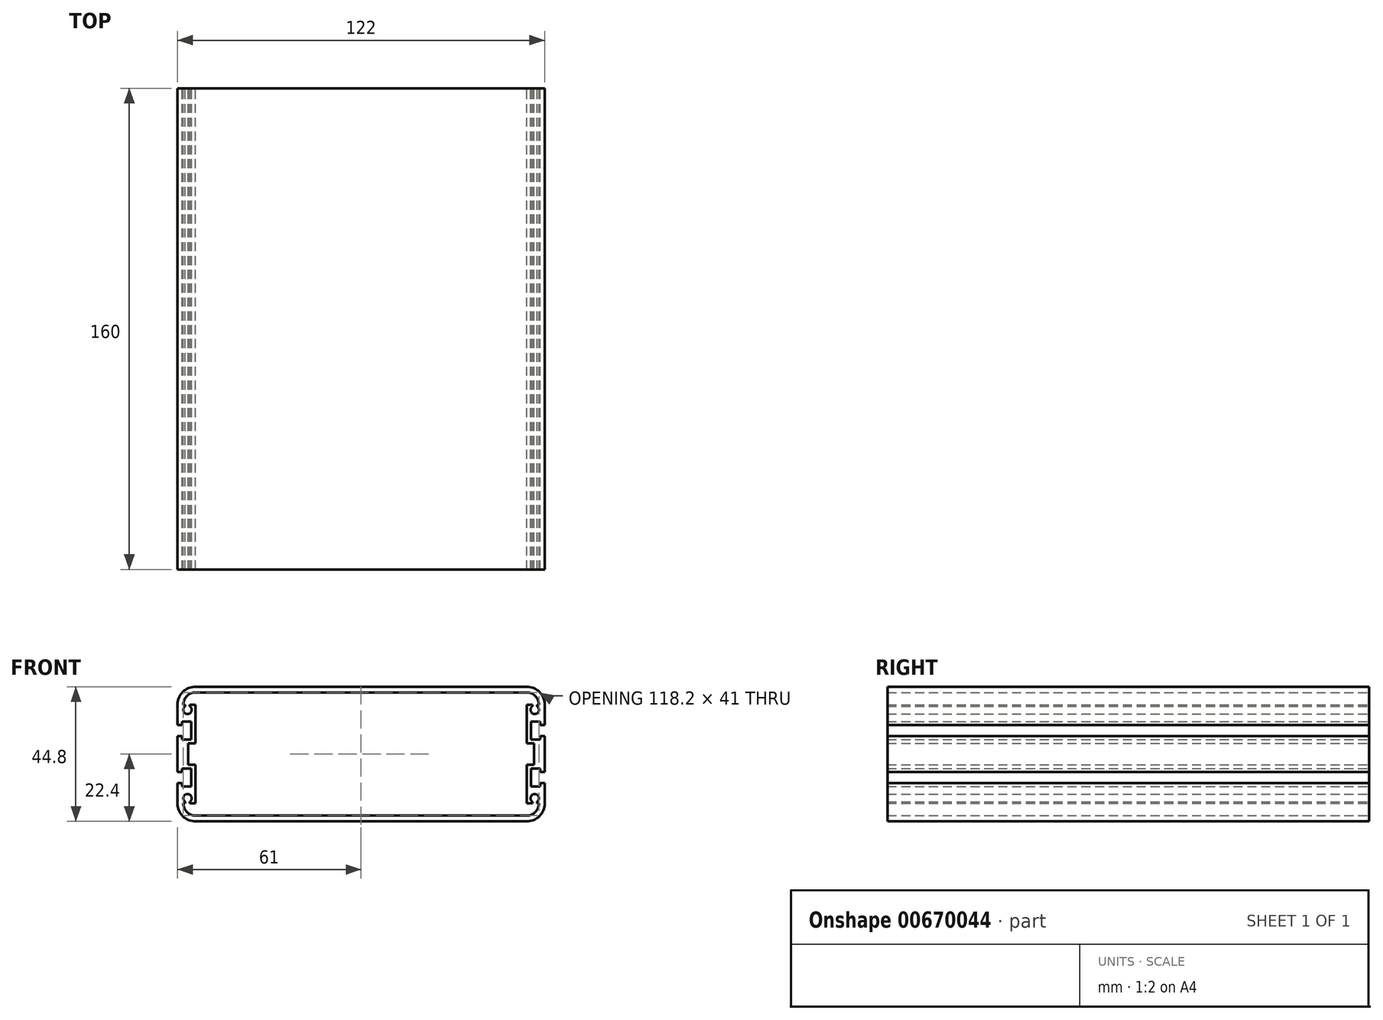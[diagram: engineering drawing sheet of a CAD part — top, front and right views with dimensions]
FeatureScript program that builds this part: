
annotation { "Feature Type Name" : "Feature", "Feature Type Description" : "" }
export const myFeature = defineFeature(function(context is Context, id is Id, definition is map)
    precondition{}
    {
        {
            var Q0;
            Q0=qCreatedBy(makeId("Front.planeOp"),FACE);
            var sketch = newSketch(context, id + "F0", { "sketchPlane" : qUnion([Q0])});
            skLineSegment(sketch, "E0.bottom", {"start": v(0, 0) * mm, "end": v(122, 0) * mm});
            skLineSegment(sketch, "E0.top", {"start": v(6, 44.8) * mm, "end": v(61, 44.8) * mm});
            skLineSegment(sketch, "E0.left", {"start": v(0, 22.4) * mm, "end": v(0, 28.4) * mm});
            skLineSegment(sketch, "E1", {"start": v(61, 44.8) * mm, "end": v(61, 0) * mm, "construction": true});
            skLineSegment(sketch, "E2", {"start": v(0, 22.4) * mm, "end": v(122, 22.4) * mm, "construction": true});
            skLineSegment(sketch, "E3.bottom", {"start": v(6, 42.9) * mm, "end": v(61, 42.9) * mm});
            skLineSegment(sketch, "E3.left", {"start": v(6, 38.8) * mm, "end": v(6, 25.9) * mm});
            skPoint(sketch, "E3.middle", {"position": v(61, 22.4) * mm});
            skPoint(sketch, "E4.visualSharp", {"position": v(0, 44.8) * mm});
            skArc(sketch, "E4.filletArc", {"start": v(6, 44.8) * mm, "mid": v(1.76, 43.04) * mm, "end": v(0, 38.8) * mm});
            skLineSegment(sketch, "E5", {"start": v(0, 32) * mm, "end": v(1.5, 32) * mm});
            skLineSegment(sketch, "E6", {"start": v(1.5, 32) * mm, "end": v(1.5, 33.2) * mm});
            skLineSegment(sketch, "E7", {"start": v(1.5, 33.2) * mm, "end": v(4.5, 33.2) * mm});
            skLineSegment(sketch, "E8", {"start": v(4.5, 33.2) * mm, "end": v(4.5, 27.2) * mm});
            skLineSegment(sketch, "E9", {"start": v(4.5, 27.2) * mm, "end": v(1.5, 27.2) * mm});
            skLineSegment(sketch, "E10", {"start": v(1.5, 27.2) * mm, "end": v(1.5, 28.4) * mm});
            skLineSegment(sketch, "E11", {"start": v(1.5, 28.4) * mm, "end": v(0, 28.4) * mm});
            skLineSegment(sketch, "E12.trimOffspring", {"start": v(0, 32) * mm, "end": v(0, 38.8) * mm});
            skArc(sketch, "E13", {"start": v(2.55, 38.28) * mm, "mid": v(3.3, 35.7) * mm, "end": v(4.05, 38.28) * mm});
            skArc(sketch, "E14", {"start": v(6, 42.9) * mm, "mid": v(3.1, 41.7) * mm, "end": v(1.9, 38.8) * mm});
            skLineSegment(sketch, "E15", {"start": v(1.9, 38.8) * mm, "end": v(2.55, 38.8) * mm});
            skLineSegment(sketch, "E16", {"start": v(2.55, 38.8) * mm, "end": v(2.55, 38.28) * mm});
            skLineSegment(sketch, "E17", {"start": v(4.05, 38.28) * mm, "end": v(4.05, 38.8) * mm});
            skLineSegment(sketch, "E18", {"start": v(4.05, 38.8) * mm, "end": v(6, 38.8) * mm});
            skLineSegment(sketch, "E19", {"start": v(3.3, 37.1) * mm, "end": v(3.3, 38.82) * mm, "construction": true});
            skLineSegment(sketch, "E20", {"start": v(3.5, 22.4) * mm, "end": v(3.5, 25.9) * mm});
            skLineSegment(sketch, "E21", {"start": v(3.5, 25.9) * mm, "end": v(6, 25.9) * mm});
            skLineSegment(sketch, "E22.MirrorCS", {"start": v(117.95, 38.28) * mm, "end": v(117.95, 38.8) * mm});
            skLineSegment(sketch, "E23.MirrorCS", {"start": v(119.45, 38.8) * mm, "end": v(119.45, 38.28) * mm});
            skLineSegment(sketch, "E24.MirrorCS", {"start": v(118.7, 37.1) * mm, "end": v(118.7, 38.82) * mm, "construction": true});
            skLineSegment(sketch, "E25.MirrorCS", {"start": v(120.1, 38.8) * mm, "end": v(119.45, 38.8) * mm});
            skLineSegment(sketch, "E26.MirrorCS", {"start": v(117.95, 38.8) * mm, "end": v(116, 38.8) * mm});
            skLineSegment(sketch, "E27.MirrorCS", {"start": v(122, 32) * mm, "end": v(120.5, 32) * mm});
            skArc(sketch, "E28.MirrorCS", {"start": v(119.45, 38.28) * mm, "mid": v(118.7, 35.7) * mm, "end": v(117.95, 38.28) * mm});
            skLineSegment(sketch, "E29.MirrorCS", {"start": v(120.5, 27.2) * mm, "end": v(120.5, 28.4) * mm});
            skLineSegment(sketch, "E30.MirrorCS", {"start": v(120.5, 32) * mm, "end": v(120.5, 33.2) * mm});
            skLineSegment(sketch, "E31.MirrorCS", {"start": v(120.5, 28.4) * mm, "end": v(122, 28.4) * mm});
            skLineSegment(sketch, "E32.MirrorCS", {"start": v(117.5, 27.2) * mm, "end": v(120.5, 27.2) * mm});
            skLineSegment(sketch, "E33.MirrorCS", {"start": v(120.5, 33.2) * mm, "end": v(117.5, 33.2) * mm});
            skLineSegment(sketch, "E34.MirrorCS", {"start": v(122, 32) * mm, "end": v(122, 38.8) * mm});
            skLineSegment(sketch, "E35.MirrorCS", {"start": v(118.5, 25.9) * mm, "end": v(116, 25.9) * mm});
            skLineSegment(sketch, "E36.MirrorCS", {"start": v(122, 22.4) * mm, "end": v(122, 28.4) * mm});
            skLineSegment(sketch, "E37.MirrorCS", {"start": v(117.5, 33.2) * mm, "end": v(117.5, 27.2) * mm});
            skArc(sketch, "E38.MirrorCS", {"start": v(116, 42.9) * mm, "mid": v(118.9, 41.7) * mm, "end": v(120.1, 38.8) * mm});
            skArc(sketch, "E39.MirrorCS", {"start": v(116, 44.8) * mm, "mid": v(120.24, 43.04) * mm, "end": v(122, 38.8) * mm});
            skLineSegment(sketch, "E40.MirrorCS", {"start": v(118.5, 22.4) * mm, "end": v(118.5, 25.9) * mm});
            skLineSegment(sketch, "E41.MirrorCS", {"start": v(116, 42.9) * mm, "end": v(61, 42.9) * mm});
            skLineSegment(sketch, "E42.MirrorCS", {"start": v(116, 38.8) * mm, "end": v(116, 25.9) * mm});
            skPoint(sketch, "E43.MirrorP", {"position": v(122, 44.8) * mm});
            skLineSegment(sketch, "E44.MirrorCS", {"start": v(116, 44.8) * mm, "end": v(61, 44.8) * mm});
            skLineSegment(sketch, "E45.MirrorCS", {"start": v(122, 22.4) * mm, "end": v(0, 22.4) * mm, "construction": true});
            skLineSegment(sketch, "E46.MirrorCS", {"start": v(2.55, 6) * mm, "end": v(2.55, 6.52) * mm});
            skLineSegment(sketch, "E47.MirrorCS", {"start": v(4.05, 6.52) * mm, "end": v(4.05, 6) * mm});
            skLineSegment(sketch, "E48.MirrorCS", {"start": v(3.3, 7.7) * mm, "end": v(3.3, 5.98) * mm, "construction": true});
            skLineSegment(sketch, "E49.MirrorCS", {"start": v(117.95, 6.52) * mm, "end": v(117.95, 6) * mm});
            skLineSegment(sketch, "E50.MirrorCS", {"start": v(1.9, 6) * mm, "end": v(2.55, 6) * mm});
            skLineSegment(sketch, "E51.MirrorCS", {"start": v(119.45, 6) * mm, "end": v(119.45, 6.52) * mm});
            skLineSegment(sketch, "E52.MirrorCS", {"start": v(117.95, 6) * mm, "end": v(116, 6) * mm});
            skLineSegment(sketch, "E53.MirrorCS", {"start": v(120.1, 6) * mm, "end": v(119.45, 6) * mm});
            skLineSegment(sketch, "E54.MirrorCS", {"start": v(0, 12.8) * mm, "end": v(1.5, 12.8) * mm});
            skLineSegment(sketch, "E55.MirrorCS", {"start": v(1.5, 17.6) * mm, "end": v(1.5, 16.4) * mm});
            skLineSegment(sketch, "E56.MirrorCS", {"start": v(1.5, 16.4) * mm, "end": v(0, 16.4) * mm});
            skLineSegment(sketch, "E57.MirrorCS", {"start": v(1.5, 12.8) * mm, "end": v(1.5, 11.6) * mm});
            skLineSegment(sketch, "E58.MirrorCS", {"start": v(4.05, 6) * mm, "end": v(6, 6) * mm});
            skLineSegment(sketch, "E59.MirrorCS", {"start": v(118.7, 7.7) * mm, "end": v(118.7, 5.98) * mm, "construction": true});
            skLineSegment(sketch, "E60.MirrorCS", {"start": v(122, 12.8) * mm, "end": v(120.5, 12.8) * mm});
            skArc(sketch, "E61.MirrorCS", {"start": v(2.55, 6.52) * mm, "mid": v(3.3, 9.1) * mm, "end": v(4.05, 6.52) * mm});
            skLineSegment(sketch, "E62.MirrorCS", {"start": v(120.5, 17.6) * mm, "end": v(120.5, 16.4) * mm});
            skLineSegment(sketch, "E63.MirrorCS", {"start": v(120.5, 12.8) * mm, "end": v(120.5, 11.6) * mm});
            skLineSegment(sketch, "E64.MirrorCS", {"start": v(4.5, 17.6) * mm, "end": v(1.5, 17.6) * mm});
            skLineSegment(sketch, "E65.MirrorCS", {"start": v(120.5, 16.4) * mm, "end": v(122, 16.4) * mm});
            skLineSegment(sketch, "E66.MirrorCS", {"start": v(1.5, 11.6) * mm, "end": v(4.5, 11.6) * mm});
            skLineSegment(sketch, "E67.MirrorCS", {"start": v(3.5, 18.9) * mm, "end": v(6, 18.9) * mm});
            skLineSegment(sketch, "E68.MirrorCS", {"start": v(120.5, 11.6) * mm, "end": v(117.5, 11.6) * mm});
            skLineSegment(sketch, "E69.MirrorCS", {"start": v(117.5, 17.6) * mm, "end": v(120.5, 17.6) * mm});
            skLineSegment(sketch, "E70.MirrorCS", {"start": v(122, 22.4) * mm, "end": v(122, 16.4) * mm});
            skLineSegment(sketch, "E71.MirrorCS", {"start": v(6, 6) * mm, "end": v(6, 18.9) * mm});
            skArc(sketch, "E72.MirrorCS", {"start": v(119.45, 6.52) * mm, "mid": v(118.7, 9.1) * mm, "end": v(117.95, 6.52) * mm});
            skLineSegment(sketch, "E73.MirrorCS", {"start": v(0, 22.4) * mm, "end": v(0, 16.4) * mm});
            skLineSegment(sketch, "E74.MirrorCS", {"start": v(116, 6) * mm, "end": v(116, 18.9) * mm});
            skLineSegment(sketch, "E75.MirrorCS", {"start": v(118.5, 18.9) * mm, "end": v(116, 18.9) * mm});
            skLineSegment(sketch, "E76.MirrorCS", {"start": v(4.5, 11.6) * mm, "end": v(4.5, 17.6) * mm});
            skLineSegment(sketch, "E77.MirrorCS", {"start": v(117.5, 11.6) * mm, "end": v(117.5, 17.6) * mm});
            skArc(sketch, "E78.MirrorCS", {"start": v(116, 1.9) * mm, "mid": v(118.9, 3.1) * mm, "end": v(120.1, 6) * mm});
            skLineSegment(sketch, "E79.MirrorCS", {"start": v(3.5, 22.4) * mm, "end": v(3.5, 18.9) * mm});
            skLineSegment(sketch, "E80.MirrorCS", {"start": v(118.5, 22.4) * mm, "end": v(118.5, 18.9) * mm});
            skArc(sketch, "E81.MirrorCS", {"start": v(6, 0) * mm, "mid": v(1.76, 1.76) * mm, "end": v(0, 6) * mm});
            skArc(sketch, "E82.MirrorCS", {"start": v(6, 1.9) * mm, "mid": v(3.1, 3.1) * mm, "end": v(1.9, 6) * mm});
            skArc(sketch, "E83.MirrorCS", {"start": v(116, 0) * mm, "mid": v(120.24, 1.76) * mm, "end": v(122, 6) * mm});
            skLineSegment(sketch, "E84.MirrorCS", {"start": v(0, 12.8) * mm, "end": v(0, 6) * mm});
            skPoint(sketch, "E85.MirrorP", {"position": v(0, 0) * mm});
            skLineSegment(sketch, "E86.MirrorCS", {"start": v(116, 0) * mm, "end": v(61, 0) * mm});
            skLineSegment(sketch, "E87.MirrorCS", {"start": v(122, 12.8) * mm, "end": v(122, 6) * mm});
            skLineSegment(sketch, "E88.MirrorCS", {"start": v(6, 0) * mm, "end": v(61, 0) * mm});
            skLineSegment(sketch, "E89.MirrorCS", {"start": v(6, 1.9) * mm, "end": v(61, 1.9) * mm});
            skLineSegment(sketch, "E90.MirrorCS", {"start": v(116, 1.9) * mm, "end": v(61, 1.9) * mm});
            skPoint(sketch, "E91.MirrorP", {"position": v(122, 0) * mm});
            skSolve(sketch);
        }
        {
            var Q0;
            Q0 = qSketchRegion(id + "F0", true);
            extrude(context, id + "F1", {"entities" : qUnion([Q0]), "depth" : 160 * mm, "offsetDistance" : 25 * mm});
        }
    });
